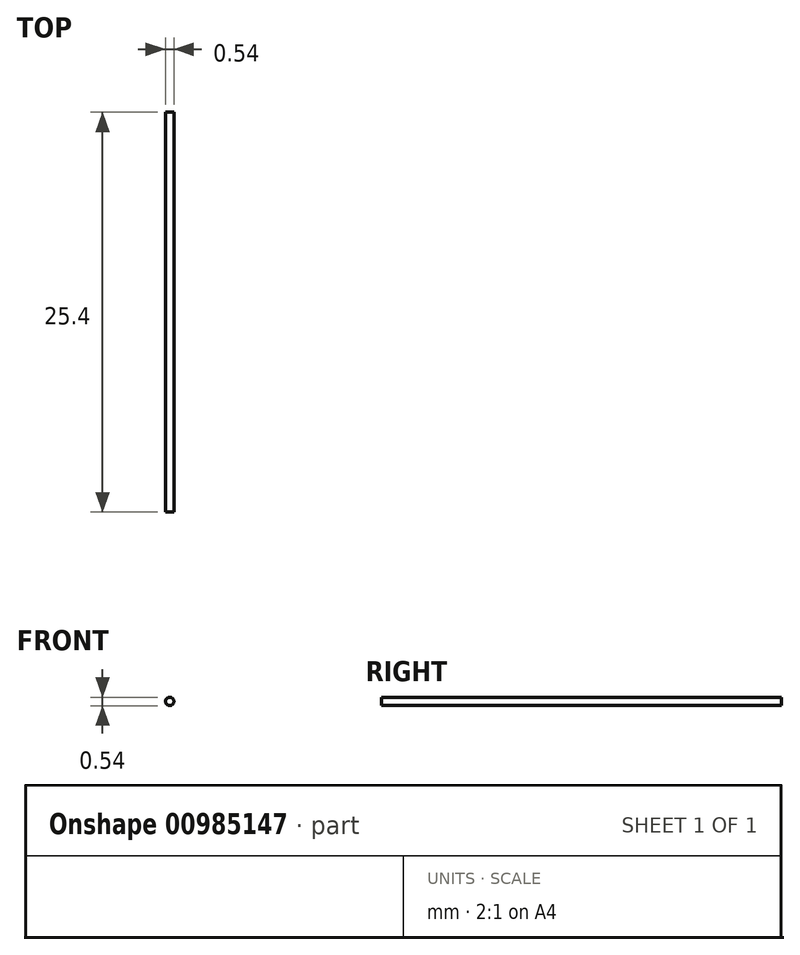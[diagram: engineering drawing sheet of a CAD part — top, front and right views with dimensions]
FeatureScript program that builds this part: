
annotation { "Feature Type Name" : "Feature", "Feature Type Description" : "" }
export const myFeature = defineFeature(function(context is Context, id is Id, definition is map)
    precondition{}
    {
        {
            var Q0;
            Q0=qCreatedBy(makeId("Front.planeOp"),FACE);
            var sketch = newSketch(context, id + "F0", { "sketchPlane" : qUnion([Q0])});
            skCircle(sketch, "E0", {"center": v(0, 0) * mm, "radius": 0.27 * mm});
            skSolve(sketch);
        }
        {
            var Q0;
            Q0 = qSketchRegion(id + "F0", true);
            extrude(context, id + "F1", {"entities" : qUnion([Q0]), "depth" : 25.4 * mm, "offsetDistance" : 25.4 * mm});
        }
    });
